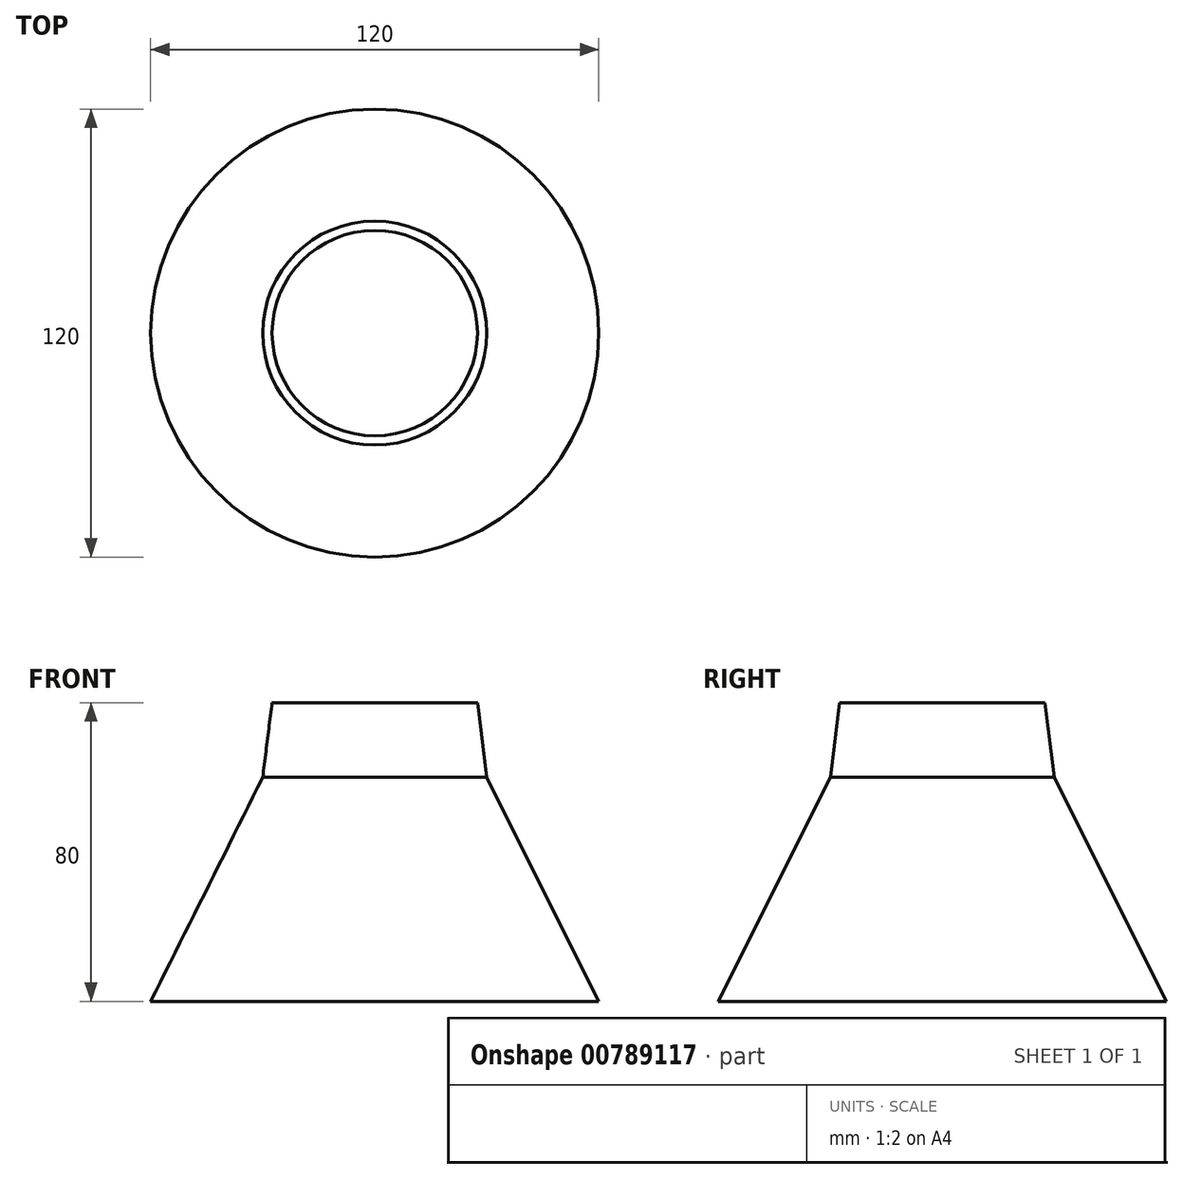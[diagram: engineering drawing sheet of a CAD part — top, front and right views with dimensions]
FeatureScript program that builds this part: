
annotation { "Feature Type Name" : "Feature", "Feature Type Description" : "" }
export const myFeature = defineFeature(function(context is Context, id is Id, definition is map)
    precondition{}
    {
        {
            var Q0;
            Q0=qCreatedBy(makeId("Right.planeOp"),FACE);
            var sketch = newSketch(context, id + "F0", { "sketchPlane" : qUnion([Q0]), "disableImprinting" : false});
            skLineSegment(sketch, "E0", {"start": v(0, 0) * mm, "end": v(0, 80) * mm});
            skLineSegment(sketch, "E1.0", {"start": v(0, 0) * mm, "end": v(60, 0) * mm});
            skLineSegment(sketch, "E2", {"start": v(60, 0) * mm, "end": v(30, 60) * mm});
            skLineSegment(sketch, "E3", {"start": v(30, 60) * mm, "end": v(27.5, 80) * mm});
            skLineSegment(sketch, "E4", {"start": v(27.5, 80) * mm, "end": v(0, 80) * mm});
            skSolve(sketch);
        }
        {
            var Q0;
            Q0 = qSketchRegion(id + "F0", true);
            var Q1;
            Q1=sQuery(id+"F0.wireOp",EDGE,"E0");
            revolve(context, id + "F1", {"surfaceOperationType" : NewSurfaceOperationType.NEW, "entities" : qUnion([Q0]), "axis" : qUnion([Q1]), "revolveType" : RevolveType.FULL});
        }
    });
